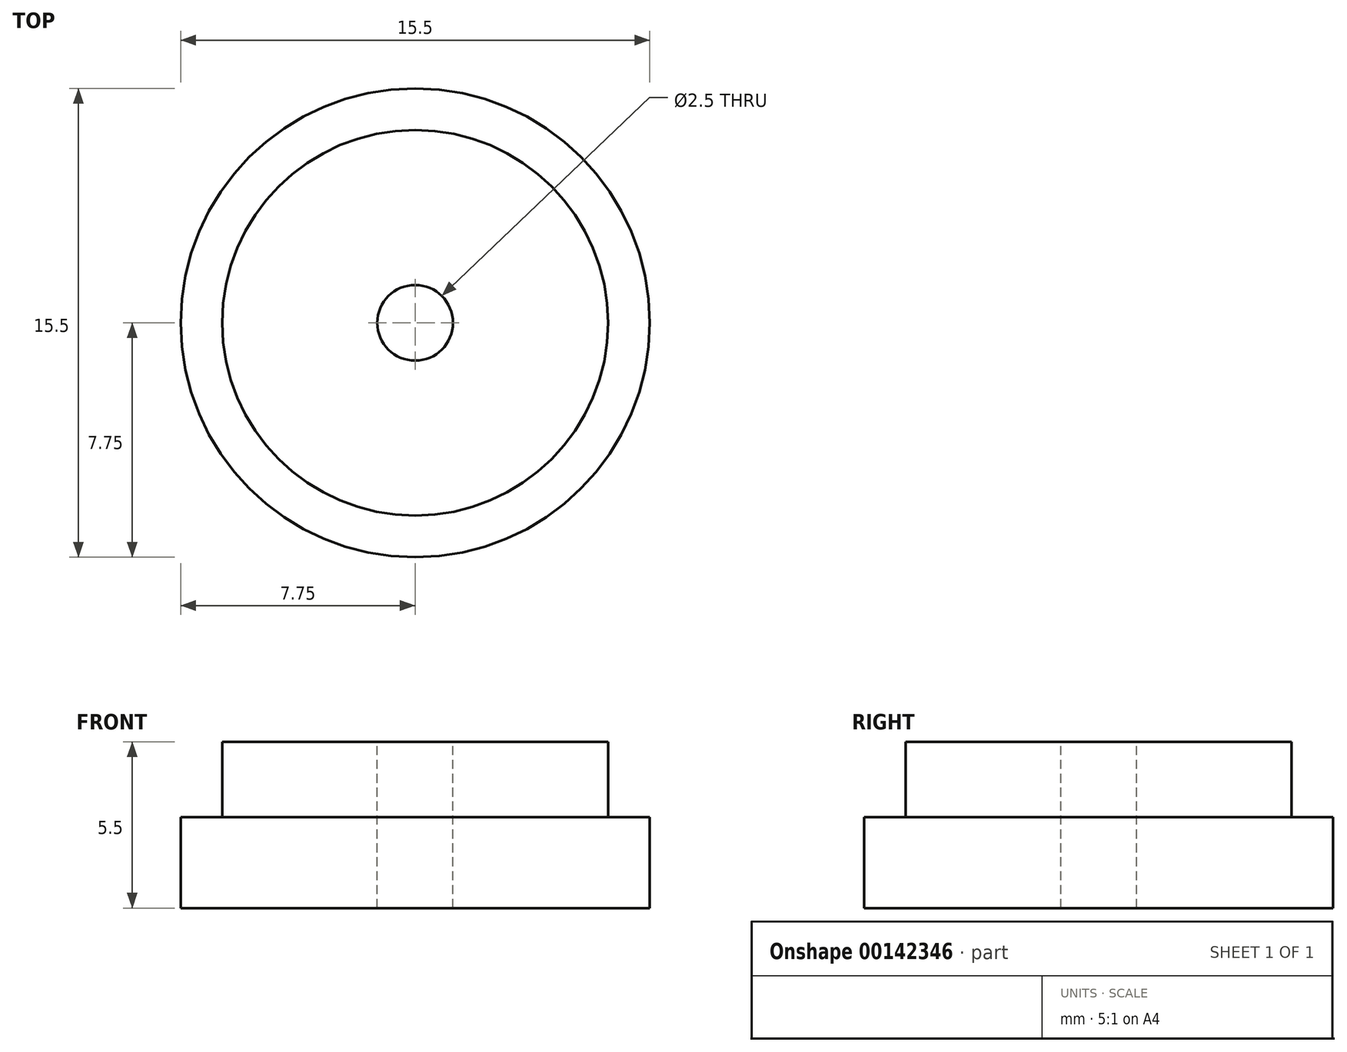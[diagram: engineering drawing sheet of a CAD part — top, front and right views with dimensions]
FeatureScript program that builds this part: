
annotation { "Feature Type Name" : "Feature", "Feature Type Description" : "" }
export const myFeature = defineFeature(function(context is Context, id is Id, definition is map)
    precondition{}
    {
        {
            var Q0;
            Q0=qCreatedBy(makeId("Top.planeOp"),FACE);
            var sketch = newSketch(context, id + "F0", { "sketchPlane" : qUnion([Q0])});
            skCircle(sketch, "E0", {"center": v(0, 0) * mm, "radius": 7.75 * mm});
            skSolve(sketch);
        }
        {
            var Q0;
            Q0=makeQuery(id+"F0.imprint","IMPRINT",FACE,{"disambiguationData":[TD([[makeQuery(id+"F0.imprint","IMPRINT",EDGE,{"derivedFrom":sQuery(id+"F0.wireOp",EDGE,"E0")}),1.0]])]});
            extrude(context, id + "F1", {"entities" : qUnion([Q0]), "depth" : 3 * mm});
        }
        {
            var Q0;
            Q0=makeQuery(id+"F1.opExtrude","CAP_FACE",FACE,{"disambiguationData":[OSD([sQuery(id+"F0.wireOp",EDGE,"E0")])],"isStart":false});
            var sketch = newSketch(context, id + "F2", { "sketchPlane" : qUnion([Q0])});
            skCircle(sketch, "E1", {"center": v(0, 0) * mm, "radius": 6.38 * mm});
            skSolve(sketch);
        }
        {
            var Q0;
            Q0=makeQuery(id+"F2.imprint","IMPRINT",FACE,{"disambiguationData":[TD([[makeQuery(id+"F2.imprint","IMPRINT",EDGE,{"derivedFrom":sQuery(id+"F2.wireOp",EDGE,"E1")}),1.0]])]});
            extrude(context, id + "F3", {"entities" : qUnion([Q0]), "operationType" : NewBodyOperationType.ADD, "depth" : 2.5 * mm});
        }
        {
            var Q0;
            Q0=makeQuery(id+"F3.opExtrude","CAP_FACE",FACE,{"disambiguationData":[OSD([sQuery(id+"F2.wireOp",EDGE,"E1")])],"isStart":false});
            var sketch = newSketch(context, id + "F4", { "sketchPlane" : qUnion([Q0])});
            skCircle(sketch, "E2", {"center": v(0, 0) * mm, "radius": 1.25 * mm});
            skSolve(sketch);
        }
        {
            var Q0;
            Q0=makeQuery(id+"F4.imprint","IMPRINT",FACE,{"disambiguationData":[TD([[makeQuery(id+"F4.imprint","IMPRINT",EDGE,{"derivedFrom":sQuery(id+"F4.wireOp",EDGE,"E2")}),1.0]])]});
            extrude(context, id + "F5", {"entities" : qUnion([Q0]), "operationType" : NewBodyOperationType.REMOVE, "oppositeDirection" : true, "depth" : 25 * mm});
        }
    });
